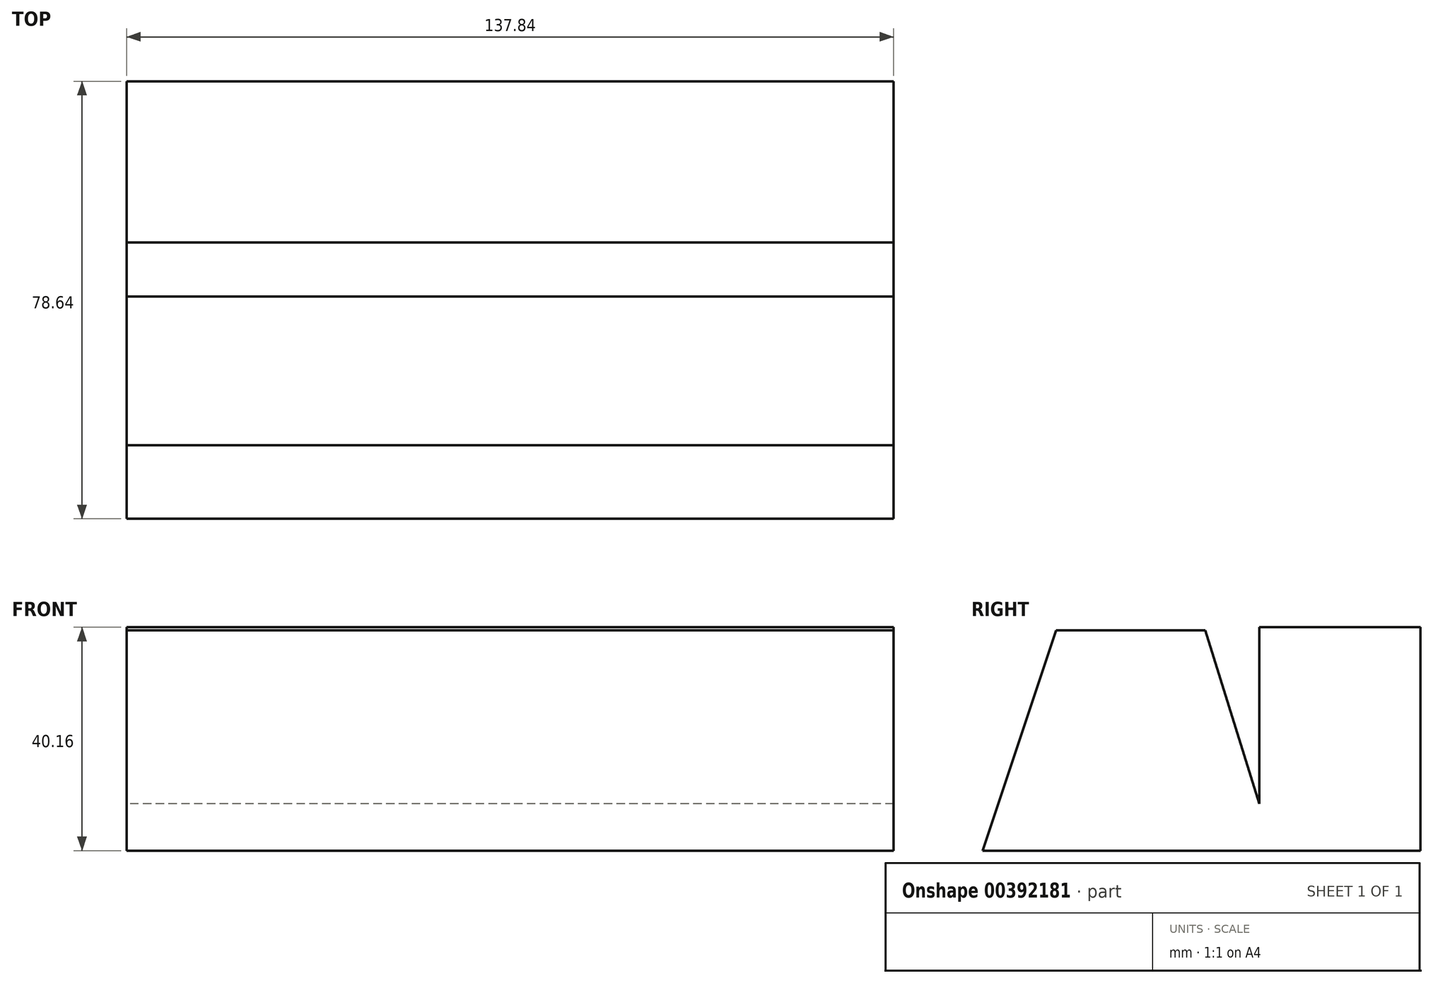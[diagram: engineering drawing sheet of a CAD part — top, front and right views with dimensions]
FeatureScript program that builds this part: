
annotation { "Feature Type Name" : "Feature", "Feature Type Description" : "" }
export const myFeature = defineFeature(function(context is Context, id is Id, definition is map)
    precondition{}
    {
        {
            var Q0;
            Q0=qCreatedBy(makeId("Right.planeOp"),FACE);
            var sketch = newSketch(context, id + "F0", { "sketchPlane" : qUnion([Q0])});
            skLineSegment(sketch, "E0", {"start": v(0, 0) * mm, "end": v(-9.72, 31.16) * mm});
            skLineSegment(sketch, "E1", {"start": v(-9.72, 31.16) * mm, "end": v(-36.48, 31.16) * mm});
            skLineSegment(sketch, "E2", {"start": v(-36.48, 31.16) * mm, "end": v(-49.68, -8.43) * mm});
            skLineSegment(sketch, "E3", {"start": v(-49.68, -8.43) * mm, "end": v(28.96, -8.43) * mm});
            skLineSegment(sketch, "E4", {"start": v(28.96, -8.43) * mm, "end": v(28.96, 31.73) * mm});
            skLineSegment(sketch, "E5", {"start": v(28.96, 31.73) * mm, "end": v(0, 31.73) * mm});
            skLineSegment(sketch, "E6", {"start": v(0, 31.73) * mm, "end": v(0, 0) * mm});
            skSolve(sketch);
        }
        {
            var Q0;
            Q0=makeQuery(id+"F0.imprint","IMPRINT",FACE,{"disambiguationData":[TD([[makeQuery(id+"F0.imprint","IMPRINT",EDGE,{"derivedFrom":sQuery(id+"F0.wireOp",EDGE,"E0")}),1.0]])]});
            var sketch = newSketch(context, id + "F1", { "sketchPlane" : qUnion([Q0])});
            skSolve(sketch);
        }
        {
            var Q0;
            Q0 = qSketchRegion(id + "F1", true);
            var Q1;
            Q1=makeQuery(id+"F1.imprint","IMPRINT",FACE,{"disambiguationData":[TD([[makeQuery(id+"F1.imprint","IMPRINT",EDGE,{"derivedFrom":makeQuery(id+"F0.imprint","IMPRINT",EDGE,{"derivedFrom":sQuery(id+"F0.wireOp",EDGE,"E0")})}),1.0]])]});
            extrude(context, id + "F2", {"entities" : qUnion([Q0, Q1]), "depth" : 137.84 * mm});
        }
    });
